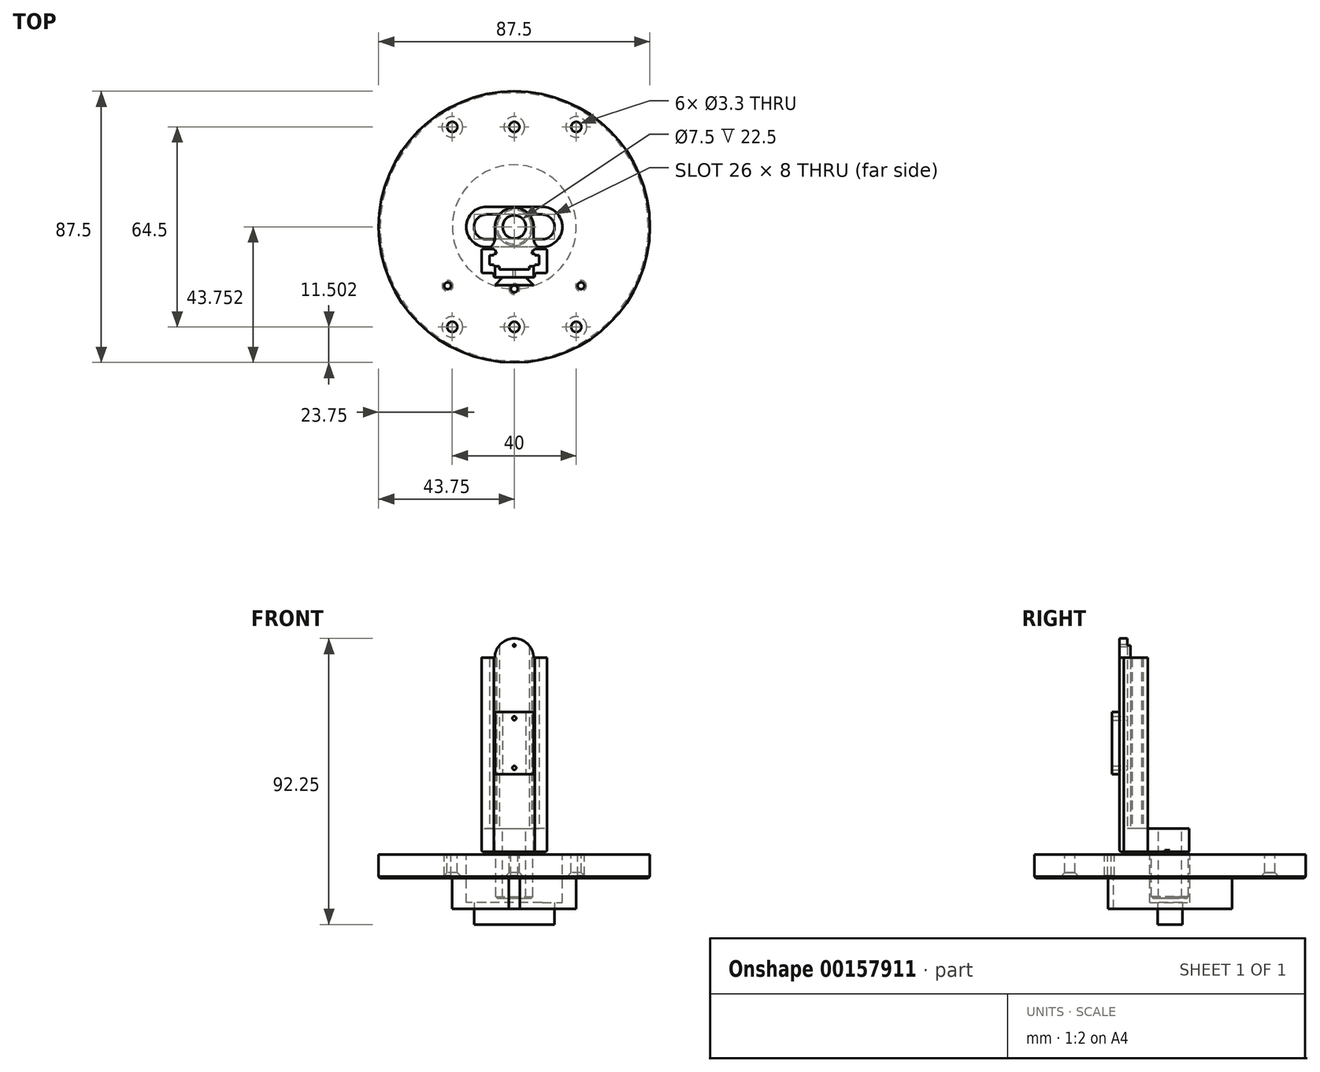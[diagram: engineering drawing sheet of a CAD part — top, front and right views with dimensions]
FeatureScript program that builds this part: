
annotation { "Feature Type Name" : "Feature", "Feature Type Description" : "" }
export const myFeature = defineFeature(function(context is Context, id is Id, definition is map)
    precondition{}
    {
        {
            var Q0;
            Q0=qCreatedBy(makeId("Top.planeOp"),FACE);
            var sketch = newSketch(context, id + "F0", { "sketchPlane" : qUnion([Q0])});
            skLineSegment(sketch, "E0.top", {"start": v(-6.65, -1.47) * mm, "end": v(-4.85, -1.47) * mm});
            skLineSegment(sketch, "E0.left", {"start": v(-8.05, 2.13) * mm, "end": v(-8.05, -0.97) * mm});
            skLineSegment(sketch, "E0.right", {"start": v(8.05, 2.13) * mm, "end": v(8.05, -0.97) * mm});
            skLineSegment(sketch, "E1", {"start": v(6.65, 2.63) * mm, "end": v(6.65, 2.13) * mm});
            skLineSegment(sketch, "E2", {"start": v(-6.65, 2.63) * mm, "end": v(-6.65, 2.13) * mm});
            skLineSegment(sketch, "E3", {"start": v(-4.85, -2.47) * mm, "end": v(4.85, -2.47) * mm});
            skLineSegment(sketch, "E4", {"start": v(6.65, 2.13) * mm, "end": v(8.05, 2.13) * mm});
            skLineSegment(sketch, "E5", {"start": v(-8.05, 2.13) * mm, "end": v(-6.65, 2.13) * mm});
            skLineSegment(sketch, "E6.MirrorCS", {"start": v(-8.05, -0.97) * mm, "end": v(-6.65, -0.97) * mm});
            skLineSegment(sketch, "E7.MirrorCS", {"start": v(6.65, -0.97) * mm, "end": v(8.05, -0.97) * mm});
            skLineSegment(sketch, "E8.trimOffspring", {"start": v(-6.65, -0.97) * mm, "end": v(-6.65, -1.47) * mm});
            skLineSegment(sketch, "E9.trimOffspring", {"start": v(6.65, -0.97) * mm, "end": v(6.65, -1.47) * mm});
            skLineSegment(sketch, "E10", {"start": v(-4.85, -1.47) * mm, "end": v(-4.85, -2.47) * mm});
            skLineSegment(sketch, "E11", {"start": v(4.85, -1.47) * mm, "end": v(4.85, -2.47) * mm});
            skLineSegment(sketch, "E12.trimOffspring", {"start": v(4.85, -1.47) * mm, "end": v(6.65, -1.47) * mm});
            skLineSegment(sketch, "E13", {"start": v(-10.55, 3.63) * mm, "end": v(-10.55, -3.14) * mm});
            skLineSegment(sketch, "E14", {"start": v(-10.05, 4.13) * mm, "end": v(-6.65, 4.13) * mm});
            skLineSegment(sketch, "E15", {"start": v(-6.15, -4.97) * mm, "end": v(6.15, -4.97) * mm});
            skLineSegment(sketch, "E16", {"start": v(10.55, -3.14) * mm, "end": v(10.55, 3.63) * mm});
            skLineSegment(sketch, "E17", {"start": v(10.05, 4.13) * mm, "end": v(6.65, 4.13) * mm});
            skPoint(sketch, "E18.visualSharp", {"position": v(10.55, 4.13) * mm});
            skArc(sketch, "E18.filletArc", {"start": v(10.55, 3.63) * mm, "mid": v(10.4, 3.99) * mm, "end": v(10.05, 4.13) * mm});
            skPoint(sketch, "E19.visualSharp", {"position": v(-10.55, 4.13) * mm});
            skArc(sketch, "E19.filletArc", {"start": v(-10.05, 4.13) * mm, "mid": v(-10.4, 3.99) * mm, "end": v(-10.55, 3.63) * mm});
            skLineSegment(sketch, "E20", {"start": v(-10.05, -3.64) * mm, "end": v(-7.15, -3.64) * mm});
            skLineSegment(sketch, "E21", {"start": v(6.65, -4.14) * mm, "end": v(6.65, -4.47) * mm});
            skLineSegment(sketch, "E22", {"start": v(-6.65, -4.14) * mm, "end": v(-6.65, -4.47) * mm});
            skLineSegment(sketch, "E23.trimOffspring", {"start": v(7.15, -3.64) * mm, "end": v(10.05, -3.64) * mm});
            skPoint(sketch, "E24.visualSharp", {"position": v(-10.55, -3.64) * mm});
            skArc(sketch, "E24.filletArc", {"start": v(-10.55, -3.14) * mm, "mid": v(-10.4, -3.49) * mm, "end": v(-10.05, -3.64) * mm});
            skPoint(sketch, "E25.visualSharp", {"position": v(-6.65, -3.64) * mm});
            skArc(sketch, "E25.filletArc", {"start": v(-6.65, -4.14) * mm, "mid": v(-6.8, -3.78) * mm, "end": v(-7.15, -3.64) * mm});
            skPoint(sketch, "E26.visualSharp", {"position": v(-6.65, -4.97) * mm});
            skArc(sketch, "E26.filletArc", {"start": v(-6.65, -4.47) * mm, "mid": v(-6.5, -4.82) * mm, "end": v(-6.15, -4.97) * mm});
            skPoint(sketch, "E27.visualSharp", {"position": v(6.65, -4.97) * mm});
            skArc(sketch, "E27.filletArc", {"start": v(6.15, -4.97) * mm, "mid": v(6.5, -4.82) * mm, "end": v(6.65, -4.47) * mm});
            skPoint(sketch, "E28.visualSharp", {"position": v(6.65, -3.64) * mm});
            skArc(sketch, "E28.filletArc", {"start": v(7.15, -3.64) * mm, "mid": v(6.8, -3.78) * mm, "end": v(6.65, -4.14) * mm});
            skPoint(sketch, "E29.visualSharp", {"position": v(10.55, -3.64) * mm});
            skArc(sketch, "E29.filletArc", {"start": v(10.05, -3.64) * mm, "mid": v(10.4, -3.49) * mm, "end": v(10.55, -3.14) * mm});
            skLineSegment(sketch, "E30", {"start": v(-6.65, 4.13) * mm, "end": v(-6.65, 3.88) * mm});
            skLineSegment(sketch, "E31", {"start": v(-6.65, 3.88) * mm, "end": v(-6.15, 3.88) * mm});
            skLineSegment(sketch, "E32", {"start": v(0, -2.47) * mm, "end": v(0, -1.47) * mm});
            skLineSegment(sketch, "E33.MirrorCS", {"start": v(6.65, 3.88) * mm, "end": v(6.15, 3.88) * mm});
            skLineSegment(sketch, "E34.MirrorCS", {"start": v(6.65, 4.13) * mm, "end": v(6.65, 3.88) * mm});
            skLineSegment(sketch, "E35", {"start": v(-6.65, 2.63) * mm, "end": v(-5.65, 2.63) * mm});
            skLineSegment(sketch, "E36", {"start": v(-6.15, 3.88) * mm, "end": v(-5.65, 2.63) * mm});
            skLineSegment(sketch, "E37.MirrorCS", {"start": v(6.65, 2.63) * mm, "end": v(5.65, 2.63) * mm});
            skLineSegment(sketch, "E38.MirrorCS", {"start": v(6.15, 3.88) * mm, "end": v(5.65, 2.63) * mm});
            skLineSegment(sketch, "E39", {"start": v(-8.05, 0.58) * mm, "end": v(-8.8, 0.58) * mm});
            skSolve(sketch);
        }
        {
            var Q0;
            Q0=makeQuery(id+"F0.imprint","IMPRINT",FACE,{"disambiguationData":[TD([[makeQuery(id+"F0.imprint","IMPRINT",EDGE,{"derivedFrom":sQuery(id+"F0.wireOp",EDGE,"E0.top")}),-1.0]])]});
            extrude(context, id + "F1", {"entities" : qUnion([Q0]), "depth" : 55 * mm, "symmetric" : true});
        }
        {
            var Q0;
            Q0=qCreatedBy(makeId("Top.planeOp"),FACE);
            var sketch = newSketch(context, id + "F2", { "sketchPlane" : qUnion([Q0])});
            skLineSegment(sketch, "E40.0", {"start": v(-3.75, -4.97) * mm, "end": v(3.75, -4.97) * mm});
            skLineSegment(sketch, "E41", {"start": v(-6.25, -7.47) * mm, "end": v(6.25, -7.47) * mm});
            skLineSegment(sketch, "E42", {"start": v(6.25, -7.47) * mm, "end": v(3.75, -4.97) * mm});
            skLineSegment(sketch, "E43.MirrorCS", {"start": v(-6.25, -7.47) * mm, "end": v(-3.75, -4.97) * mm});
            skPoint(sketch, "E44.orphan", {"position": v(6.15, -4.97) * mm});
            skPoint(sketch, "E45.orphan", {"position": v(-6.15, -4.97) * mm});
            skSolve(sketch);
        }
        {
            var Q0;
            Q0 = qSketchRegion(id + "F2", true);
            extrude(context, id + "F3", {"entities" : qUnion([Q0]), "operationType" : NewBodyOperationType.ADD, "depth" : 20 * mm, "symmetric" : true});
        }
        {
            var Q0;
            Q0=makeQuery(id+"F1.opExtrude","CAP_FACE",FACE,{"disambiguationData":[OSD([sQuery(id+"F0.wireOp",EDGE,"E0.top"),sQuery(id+"F0.wireOp",EDGE,"E0.left"),sQuery(id+"F0.wireOp",EDGE,"E0.right"),sQuery(id+"F0.wireOp",EDGE,"E1"),sQuery(id+"F0.wireOp",EDGE,"E2"),sQuery(id+"F0.wireOp",EDGE,"E3"),sQuery(id+"F0.wireOp",EDGE,"E4"),sQuery(id+"F0.wireOp",EDGE,"E5"),sQuery(id+"F0.wireOp",EDGE,"E6.MirrorCS"),sQuery(id+"F0.wireOp",EDGE,"E7.MirrorCS"),sQuery(id+"F0.wireOp",EDGE,"E8.trimOffspring"),sQuery(id+"F0.wireOp",EDGE,"E9.trimOffspring"),sQuery(id+"F0.wireOp",EDGE,"E10"),sQuery(id+"F0.wireOp",EDGE,"E11"),sQuery(id+"F0.wireOp",EDGE,"E12.trimOffspring"),sQuery(id+"F0.wireOp",EDGE,"E13"),sQuery(id+"F0.wireOp",EDGE,"E14"),sQuery(id+"F0.wireOp",EDGE,"E15"),sQuery(id+"F0.wireOp",EDGE,"E16"),sQuery(id+"F0.wireOp",EDGE,"E17"),sQuery(id+"F0.wireOp",EDGE,"E18.filletArc"),sQuery(id+"F0.wireOp",EDGE,"E19.filletArc"),sQuery(id+"F0.wireOp",EDGE,"E20"),sQuery(id+"F0.wireOp",EDGE,"E21"),sQuery(id+"F0.wireOp",EDGE,"E22"),sQuery(id+"F0.wireOp",EDGE,"E23.trimOffspring"),sQuery(id+"F0.wireOp",EDGE,"E24.filletArc"),sQuery(id+"F0.wireOp",EDGE,"E25.filletArc"),sQuery(id+"F0.wireOp",EDGE,"E26.filletArc"),sQuery(id+"F0.wireOp",EDGE,"E27.filletArc"),sQuery(id+"F0.wireOp",EDGE,"E28.filletArc"),sQuery(id+"F0.wireOp",EDGE,"E29.filletArc"),sQuery(id+"F0.wireOp",EDGE,"E30"),sQuery(id+"F0.wireOp",EDGE,"E31"),sQuery(id+"F0.wireOp",EDGE,"E33.MirrorCS"),sQuery(id+"F0.wireOp",EDGE,"E34.MirrorCS"),sQuery(id+"F0.wireOp",EDGE,"E35"),sQuery(id+"F0.wireOp",EDGE,"E36"),sQuery(id+"F0.wireOp",EDGE,"E37.MirrorCS"),sQuery(id+"F0.wireOp",EDGE,"E38.MirrorCS")])],"isStart":true});
            var sketch = newSketch(context, id + "F4", { "sketchPlane" : qUnion([Q0])});
            skLineSegment(sketch, "E46.0", {"start": v(-6.15, 4.97) * mm, "end": v(6.15, 4.97) * mm});
            skLineSegment(sketch, "E47.0", {"start": v(-10.05, 3.64) * mm, "end": v(-7.15, 3.64) * mm});
            skLineSegment(sketch, "E48.0", {"start": v(7.15, 3.64) * mm, "end": v(10.05, 3.64) * mm});
            skLineSegment(sketch, "E49.0", {"start": v(10.55, 3.14) * mm, "end": v(10.55, -3.63) * mm});
            skLineSegment(sketch, "E50.0", {"start": v(-10.55, -3.63) * mm, "end": v(-10.55, 3.14) * mm});
            skArc(sketch, "E51.0", {"start": v(6.15, 4.97) * mm, "mid": v(6.5, 4.82) * mm, "end": v(6.65, 4.47) * mm});
            skLineSegment(sketch, "E52.0", {"start": v(6.65, 4.14) * mm, "end": v(6.65, 4.47) * mm});
            skArc(sketch, "E53.0", {"start": v(7.15, 3.64) * mm, "mid": v(6.8, 3.78) * mm, "end": v(6.65, 4.14) * mm});
            skArc(sketch, "E54.0", {"start": v(-6.65, 4.47) * mm, "mid": v(-6.5, 4.82) * mm, "end": v(-6.15, 4.97) * mm});
            skLineSegment(sketch, "E55.0", {"start": v(-6.65, 4.14) * mm, "end": v(-6.65, 4.47) * mm});
            skArc(sketch, "E56.0", {"start": v(-6.65, 4.14) * mm, "mid": v(-6.8, 3.78) * mm, "end": v(-7.15, 3.64) * mm});
            skArc(sketch, "E57.0", {"start": v(-10.55, 3.14) * mm, "mid": v(-10.4, 3.49) * mm, "end": v(-10.05, 3.64) * mm});
            skArc(sketch, "E58.0", {"start": v(-10.05, -4.13) * mm, "mid": v(-10.4, -3.99) * mm, "end": v(-10.55, -3.63) * mm});
            skArc(sketch, "E59.0", {"start": v(10.05, 3.64) * mm, "mid": v(10.4, 3.49) * mm, "end": v(10.55, 3.14) * mm});
            skArc(sketch, "E60.0", {"start": v(10.55, -3.63) * mm, "mid": v(10.4, -3.99) * mm, "end": v(10.05, -4.13) * mm});
            skCircle(sketch, "E61", {"center": v(0, -11.28) * mm, "radius": 3.75 * mm});
            skCircle(sketch, "E62", {"center": v(0, -11.28) * mm, "radius": 6.25 * mm});
            skLineSegment(sketch, "E63", {"start": v(-6.25, -11.28) * mm, "end": v(-6.25, -7.63) * mm});
            skLineSegment(sketch, "E64", {"start": v(6.25, -11.28) * mm, "end": v(6.25, -7.63) * mm});
            skLineSegment(sketch, "E65", {"start": v(-10.05, -4.13) * mm, "end": v(-9.75, -4.13) * mm});
            skLineSegment(sketch, "E66.trimOffspring", {"start": v(9.75, -4.13) * mm, "end": v(10.05, -4.13) * mm});
            skPoint(sketch, "E67.visualSharp", {"position": v(-6.25, -4.13) * mm});
            skArc(sketch, "E67.filletArc", {"start": v(-6.25, -7.63) * mm, "mid": v(-7.28, -5.16) * mm, "end": v(-9.75, -4.13) * mm});
            skPoint(sketch, "E68.visualSharp", {"position": v(6.25, -4.13) * mm});
            skArc(sketch, "E68.filletArc", {"start": v(9.75, -4.13) * mm, "mid": v(7.28, -5.16) * mm, "end": v(6.25, -7.63) * mm});
            skSolve(sketch);
        }
        {
            var Q0;
            Q0 = qSketchRegion(id + "F4", true);
            extrude(context, id + "F5", {"entities" : qUnion([Q0]), "operationType" : NewBodyOperationType.ADD, "depth" : 7.5 * mm});
        }
        {
            var Q0;
            Q0=makeQuery(id+"F5.opExtrude","CAP_FACE",FACE,{"disambiguationData":[OSD([sQuery(id+"F4.wireOp",EDGE,"E46.0"),sQuery(id+"F4.wireOp",EDGE,"E47.0"),sQuery(id+"F4.wireOp",EDGE,"E48.0"),sQuery(id+"F4.wireOp",EDGE,"E49.0"),sQuery(id+"F4.wireOp",EDGE,"E50.0"),sQuery(id+"F4.wireOp",EDGE,"E51.0"),sQuery(id+"F4.wireOp",EDGE,"E52.0"),sQuery(id+"F4.wireOp",EDGE,"E53.0"),sQuery(id+"F4.wireOp",EDGE,"E54.0"),sQuery(id+"F4.wireOp",EDGE,"E55.0"),sQuery(id+"F4.wireOp",EDGE,"E56.0"),sQuery(id+"F4.wireOp",EDGE,"E57.0"),sQuery(id+"F4.wireOp",EDGE,"E58.0"),sQuery(id+"F4.wireOp",EDGE,"E59.0"),sQuery(id+"F4.wireOp",EDGE,"E60.0"),sQuery(id+"F4.wireOp",EDGE,"E61"),sQuery(id+"F4.wireOp",EDGE,"E62"),sQuery(id+"F4.wireOp",EDGE,"E63"),sQuery(id+"F4.wireOp",EDGE,"E64"),sQuery(id+"F4.wireOp",EDGE,"E65"),sQuery(id+"F4.wireOp",EDGE,"E66.trimOffspring"),sQuery(id+"F4.wireOp",EDGE,"E67.filletArc"),sQuery(id+"F4.wireOp",EDGE,"E68.filletArc")])],"isStart":false});
            var sketch = newSketch(context, id + "F6", { "sketchPlane" : qUnion([Q0])});
            skCircle(sketch, "E69.0", {"center": v(0, -11.28) * mm, "radius": 3.75 * mm});
            skCircle(sketch, "E70", {"center": v(0, -11.28) * mm, "radius": 6 * mm});
            skSolve(sketch);
        }
        {
            var Q0;
            Q0 = qSketchRegion(id + "F6", true);
            extrude(context, id + "F7", {"entities" : qUnion([Q0]), "operationType" : NewBodyOperationType.ADD, "depth" : 15 * mm});
        }
        {
            var Q0;
            Q0=makeQuery(id+"F5.opExtrude","CAP_EDGE",EDGE,{"disambiguationData":[OSD([sQuery(id+"F4.wireOp",EDGE,"E49.0")])],"isStart":false});
            fillet(context, id + "F8", {"entities" : qUnion([Q0]), "radius" : 0.5 * mm, "tangentPropagation" : true, "allowEdgeOverflow" : false});
        }
        {
            var Q0;
            Q0=makeQuery(id+"F7.opExtrude","CAP_EDGE",EDGE,{"disambiguationData":[OSD([sQuery(id+"F6.wireOp",EDGE,"E70")])],"isStart":false});
            chamfer(context, id + "F9", {"entities" : qUnion([Q0]), "width" : 0.5 * mm, "tangentPropagation" : true});
        }
        {
            var Q0;
            Q0=makeQuery(id+"F1.opExtrude","CAP_FACE",FACE,{"disambiguationData":[OSD([sQuery(id+"F0.wireOp",EDGE,"E0.top"),sQuery(id+"F0.wireOp",EDGE,"E0.left"),sQuery(id+"F0.wireOp",EDGE,"E0.right"),sQuery(id+"F0.wireOp",EDGE,"E1"),sQuery(id+"F0.wireOp",EDGE,"E2"),sQuery(id+"F0.wireOp",EDGE,"E3"),sQuery(id+"F0.wireOp",EDGE,"E4"),sQuery(id+"F0.wireOp",EDGE,"E5"),sQuery(id+"F0.wireOp",EDGE,"E6.MirrorCS"),sQuery(id+"F0.wireOp",EDGE,"E7.MirrorCS"),sQuery(id+"F0.wireOp",EDGE,"E8.trimOffspring"),sQuery(id+"F0.wireOp",EDGE,"E9.trimOffspring"),sQuery(id+"F0.wireOp",EDGE,"E10"),sQuery(id+"F0.wireOp",EDGE,"E11"),sQuery(id+"F0.wireOp",EDGE,"E12.trimOffspring"),sQuery(id+"F0.wireOp",EDGE,"E13"),sQuery(id+"F0.wireOp",EDGE,"E14"),sQuery(id+"F0.wireOp",EDGE,"E15"),sQuery(id+"F0.wireOp",EDGE,"E16"),sQuery(id+"F0.wireOp",EDGE,"E17"),sQuery(id+"F0.wireOp",EDGE,"E18.filletArc"),sQuery(id+"F0.wireOp",EDGE,"E19.filletArc"),sQuery(id+"F0.wireOp",EDGE,"E20"),sQuery(id+"F0.wireOp",EDGE,"E21"),sQuery(id+"F0.wireOp",EDGE,"E22"),sQuery(id+"F0.wireOp",EDGE,"E23.trimOffspring"),sQuery(id+"F0.wireOp",EDGE,"E24.filletArc"),sQuery(id+"F0.wireOp",EDGE,"E25.filletArc"),sQuery(id+"F0.wireOp",EDGE,"E26.filletArc"),sQuery(id+"F0.wireOp",EDGE,"E27.filletArc"),sQuery(id+"F0.wireOp",EDGE,"E28.filletArc"),sQuery(id+"F0.wireOp",EDGE,"E29.filletArc"),sQuery(id+"F0.wireOp",EDGE,"E30"),sQuery(id+"F0.wireOp",EDGE,"E31"),sQuery(id+"F0.wireOp",EDGE,"E33.MirrorCS"),sQuery(id+"F0.wireOp",EDGE,"E34.MirrorCS"),sQuery(id+"F0.wireOp",EDGE,"E35"),sQuery(id+"F0.wireOp",EDGE,"E36"),sQuery(id+"F0.wireOp",EDGE,"E37.MirrorCS"),sQuery(id+"F0.wireOp",EDGE,"E38.MirrorCS")])],"isStart":false});
            var sketch = newSketch(context, id + "F10", { "sketchPlane" : qUnion([Q0])});
            skLineSegment(sketch, "E71", {"start": v(6.25, -4.96) * mm, "end": v(6.25, -1.47) * mm});
            skLineSegment(sketch, "E72.0", {"start": v(-6.15, -4.97) * mm, "end": v(6.15, -4.97) * mm});
            skLineSegment(sketch, "E73.0", {"start": v(-4.85, -2.47) * mm, "end": v(4.85, -2.47) * mm});
            skLineSegment(sketch, "E74.0", {"start": v(4.85, -1.47) * mm, "end": v(6.65, -1.47) * mm});
            skLineSegment(sketch, "E75", {"start": v(4.85, -1.47) * mm, "end": v(4.85, -2.47) * mm});
            skLineSegment(sketch, "E76.MirrorCS", {"start": v(-4.85, -1.47) * mm, "end": v(-6.65, -1.47) * mm});
            skLineSegment(sketch, "E77.MirrorCS", {"start": v(-4.85, -1.47) * mm, "end": v(-4.85, -2.47) * mm});
            skLineSegment(sketch, "E78.MirrorCS", {"start": v(-6.25, -4.96) * mm, "end": v(-6.25, -1.47) * mm});
            skArc(sketch, "E79.0", {"start": v(6.15, -4.97) * mm, "mid": v(6.2, -4.97) * mm, "end": v(6.25, -4.96) * mm});
            skArc(sketch, "E80.0", {"start": v(-6.25, -4.96) * mm, "mid": v(-6.2, -4.97) * mm, "end": v(-6.15, -4.97) * mm});
            skPoint(sketch, "E81.orphan", {"position": v(-6.25, 0.76) * mm});
            skPoint(sketch, "E82.orphan", {"position": v(6.25, 0.76) * mm});
            skPoint(sketch, "E83.orphan", {"position": v(6.25, -5.79) * mm});
            skPoint(sketch, "E84.orphan", {"position": v(-6.25, -5.79) * mm});
            skPoint(sketch, "E85.orphan", {"position": v(-6.65, -4.47) * mm});
            skPoint(sketch, "E86.orphan", {"position": v(6.65, -4.47) * mm});
            skSolve(sketch);
        }
        {
            var Q0;
            Q0 = qSketchRegion(id + "F10", true);
            extrude(context, id + "F11", {"entities" : qUnion([Q0]), "operationType" : NewBodyOperationType.ADD, "depth" : 6.25 * mm});
        }
        {
            var Q0;
            Q0=makeQuery(id+"F11.boolean.opBoolean","MERGE",FACE,{"derivedFrom":[makeQuery(id+"F5.boolean.opBoolean","MERGE",FACE,{"derivedFrom":[makeQuery(id+"F1.opExtrude","SWEPT_FACE",FACE,{"disambiguationData":[OSD([sQuery(id+"F0.wireOp",EDGE,"E15")])]}),makeQuery(id+"F5.opExtrude","SWEPT_FACE",FACE,{"disambiguationData":[OSD([sQuery(id+"F4.wireOp",EDGE,"E46.0")])]})]}),makeQuery(id+"F11.opExtrude","SWEPT_FACE",FACE,{"disambiguationData":[OSD([sQuery(id+"F10.wireOp",EDGE,"E72.0")])]})]});
            var sketch = newSketch(context, id + "F12", { "sketchPlane" : qUnion([Q0])});
            skArc(sketch, "E87", {"start": v(6.25, 27.5) * mm, "mid": v(0, 33.75) * mm, "end": v(-6.25, 27.5) * mm});
            skPoint(sketch, "E87.centerSnap0", {"position": v(0, 33.75) * mm});
            skLineSegment(sketch, "E88", {"start": v(7.15, 27.5) * mm, "end": v(6.25, 27.5) * mm});
            skLineSegment(sketch, "E89", {"start": v(-7.18, 27.5) * mm, "end": v(-7.18, 34.65) * mm});
            skLineSegment(sketch, "E90", {"start": v(-7.18, 34.65) * mm, "end": v(7.15, 34.65) * mm});
            skLineSegment(sketch, "E91", {"start": v(7.15, 34.65) * mm, "end": v(7.15, 27.5) * mm});
            skPoint(sketch, "E92.orphan", {"position": v(6.15, 33.75) * mm});
            skPoint(sketch, "E93.0.start.orphan", {"position": v(-6.15, 33.75) * mm});
            skLineSegment(sketch, "E94.trimOffspring", {"start": v(-6.25, 27.5) * mm, "end": v(-7.18, 27.5) * mm});
            skPoint(sketch, "E95.0.end.orphan", {"position": v(10.05, 27.5) * mm});
            skSolve(sketch);
        }
        {
            var Q0;
            Q0 = qSketchRegion(id + "F12", true);
            extrude(context, id + "F13", {"entities" : qUnion([Q0]), "operationType" : NewBodyOperationType.REMOVE, "endBound" : BoundingType.THROUGH_ALL, "oppositeDirection" : true, "depth" : 25 * mm});
        }
        {
            var Q0;
            Q0=makeQuery(id+"F11.boolean.opBoolean","MERGE",FACE,{"derivedFrom":[makeQuery(id+"F5.boolean.opBoolean","MERGE",FACE,{"derivedFrom":[makeQuery(id+"F1.opExtrude","SWEPT_FACE",FACE,{"disambiguationData":[OSD([sQuery(id+"F0.wireOp",EDGE,"E15")])]}),makeQuery(id+"F5.opExtrude","SWEPT_FACE",FACE,{"disambiguationData":[OSD([sQuery(id+"F4.wireOp",EDGE,"E46.0")])]})]}),makeQuery(id+"F11.opExtrude","SWEPT_FACE",FACE,{"disambiguationData":[OSD([sQuery(id+"F10.wireOp",EDGE,"E72.0")])]})]});
            var sketch = newSketch(context, id + "F14", { "sketchPlane" : qUnion([Q0])});
            skLineSegment(sketch, "E96.0", {"start": v(7.15, 27.5) * mm, "end": v(10.05, 27.5) * mm});
            skPoint(sketch, "E97", {"position": v(0, 31.5) * mm});
            skSolve(sketch);
        }
        {
            var Q0;
            Q0=sQuery(id+"F14.wireOp",VERTEX,"E97");
            var Q1;
            Q1=makeQuery(id+"F1.opExtrude","SWEPT_BODY",BODY,{"disambiguationData":[OSD([sQuery(id+"F0.wireOp",EDGE,"E0.top"),sQuery(id+"F0.wireOp",EDGE,"E0.left"),sQuery(id+"F0.wireOp",EDGE,"E0.right"),sQuery(id+"F0.wireOp",EDGE,"E1"),sQuery(id+"F0.wireOp",EDGE,"E2"),sQuery(id+"F0.wireOp",EDGE,"E3"),sQuery(id+"F0.wireOp",EDGE,"E4"),sQuery(id+"F0.wireOp",EDGE,"E5"),sQuery(id+"F0.wireOp",EDGE,"E6.MirrorCS"),sQuery(id+"F0.wireOp",EDGE,"E7.MirrorCS"),sQuery(id+"F0.wireOp",EDGE,"E8.trimOffspring"),sQuery(id+"F0.wireOp",EDGE,"E9.trimOffspring"),sQuery(id+"F0.wireOp",EDGE,"E10"),sQuery(id+"F0.wireOp",EDGE,"E11"),sQuery(id+"F0.wireOp",EDGE,"E12.trimOffspring"),sQuery(id+"F0.wireOp",EDGE,"E13"),sQuery(id+"F0.wireOp",EDGE,"E14"),sQuery(id+"F0.wireOp",EDGE,"E15"),sQuery(id+"F0.wireOp",EDGE,"E16"),sQuery(id+"F0.wireOp",EDGE,"E17"),sQuery(id+"F0.wireOp",EDGE,"E18.filletArc"),sQuery(id+"F0.wireOp",EDGE,"E19.filletArc"),sQuery(id+"F0.wireOp",EDGE,"E20"),sQuery(id+"F0.wireOp",EDGE,"E21"),sQuery(id+"F0.wireOp",EDGE,"E22"),sQuery(id+"F0.wireOp",EDGE,"E23.trimOffspring"),sQuery(id+"F0.wireOp",EDGE,"E24.filletArc"),sQuery(id+"F0.wireOp",EDGE,"E25.filletArc"),sQuery(id+"F0.wireOp",EDGE,"E26.filletArc"),sQuery(id+"F0.wireOp",EDGE,"E27.filletArc"),sQuery(id+"F0.wireOp",EDGE,"E28.filletArc"),sQuery(id+"F0.wireOp",EDGE,"E29.filletArc"),sQuery(id+"F0.wireOp",EDGE,"E30"),sQuery(id+"F0.wireOp",EDGE,"E31"),sQuery(id+"F0.wireOp",EDGE,"E33.MirrorCS"),sQuery(id+"F0.wireOp",EDGE,"E34.MirrorCS"),sQuery(id+"F0.wireOp",EDGE,"E35"),sQuery(id+"F0.wireOp",EDGE,"E36"),sQuery(id+"F0.wireOp",EDGE,"E37.MirrorCS"),sQuery(id+"F0.wireOp",EDGE,"E38.MirrorCS")])]});
            hole(context, id + "F15", {"style" : HoleStyle.SIMPLE, "endStyle" : HoleEndStyle.THROUGH, "holeDiameter" : 0.75 * mm, "locations" : qUnion([Q0]), "scope" : qUnion([Q1]), "isTappedThrough" : true, "startStyle" : HoleStartStyle.SKETCH});
        }
        {
            var Q0;
            Q0=makeQuery(id+"F3.opExtrude","SWEPT_FACE",FACE,{"disambiguationData":[OSD([sQuery(id+"F2.wireOp",EDGE,"E41")])]});
            var sketch = newSketch(context, id + "F16", { "sketchPlane" : qUnion([Q0])});
            skPoint(sketch, "E98", {"position": v(0, 8) * mm});
            skPoint(sketch, "E99.MirrorP", {"position": v(0, -8) * mm});
            skSolve(sketch);
        }
        {
            var Q0;
            Q0=sQuery(id+"F16.wireOp",VERTEX,"E98");
            var Q1;
            Q1=sQuery(id+"F16.wireOp",VERTEX,"E99.MirrorP");
            var Q2;
            Q2=makeQuery(id+"F1.opExtrude","SWEPT_BODY",BODY,{"disambiguationData":[OSD([sQuery(id+"F0.wireOp",EDGE,"E0.top"),sQuery(id+"F0.wireOp",EDGE,"E0.left"),sQuery(id+"F0.wireOp",EDGE,"E0.right"),sQuery(id+"F0.wireOp",EDGE,"E1"),sQuery(id+"F0.wireOp",EDGE,"E2"),sQuery(id+"F0.wireOp",EDGE,"E3"),sQuery(id+"F0.wireOp",EDGE,"E4"),sQuery(id+"F0.wireOp",EDGE,"E5"),sQuery(id+"F0.wireOp",EDGE,"E6.MirrorCS"),sQuery(id+"F0.wireOp",EDGE,"E7.MirrorCS"),sQuery(id+"F0.wireOp",EDGE,"E8.trimOffspring"),sQuery(id+"F0.wireOp",EDGE,"E9.trimOffspring"),sQuery(id+"F0.wireOp",EDGE,"E10"),sQuery(id+"F0.wireOp",EDGE,"E11"),sQuery(id+"F0.wireOp",EDGE,"E12.trimOffspring"),sQuery(id+"F0.wireOp",EDGE,"E13"),sQuery(id+"F0.wireOp",EDGE,"E14"),sQuery(id+"F0.wireOp",EDGE,"E15"),sQuery(id+"F0.wireOp",EDGE,"E16"),sQuery(id+"F0.wireOp",EDGE,"E17"),sQuery(id+"F0.wireOp",EDGE,"E18.filletArc"),sQuery(id+"F0.wireOp",EDGE,"E19.filletArc"),sQuery(id+"F0.wireOp",EDGE,"E20"),sQuery(id+"F0.wireOp",EDGE,"E21"),sQuery(id+"F0.wireOp",EDGE,"E22"),sQuery(id+"F0.wireOp",EDGE,"E23.trimOffspring"),sQuery(id+"F0.wireOp",EDGE,"E24.filletArc"),sQuery(id+"F0.wireOp",EDGE,"E25.filletArc"),sQuery(id+"F0.wireOp",EDGE,"E26.filletArc"),sQuery(id+"F0.wireOp",EDGE,"E27.filletArc"),sQuery(id+"F0.wireOp",EDGE,"E28.filletArc"),sQuery(id+"F0.wireOp",EDGE,"E29.filletArc"),sQuery(id+"F0.wireOp",EDGE,"E30"),sQuery(id+"F0.wireOp",EDGE,"E31"),sQuery(id+"F0.wireOp",EDGE,"E33.MirrorCS"),sQuery(id+"F0.wireOp",EDGE,"E34.MirrorCS"),sQuery(id+"F0.wireOp",EDGE,"E35"),sQuery(id+"F0.wireOp",EDGE,"E36"),sQuery(id+"F0.wireOp",EDGE,"E37.MirrorCS"),sQuery(id+"F0.wireOp",EDGE,"E38.MirrorCS")])]});
            hole(context, id + "F17", {"style" : HoleStyle.SIMPLE, "endStyle" : HoleEndStyle.THROUGH, "holeDiameter" : 1.25 * mm, "locations" : qUnion([Q0, Q1]), "scope" : qUnion([Q2]), "isTappedThrough" : true, "startStyle" : HoleStartStyle.SKETCH});
        }
        {
            var Q0;
            Q0=qCreatedBy(makeId("Top.planeOp"),FACE);
            cPlane(context, id + "F18", {"entities" : qUnion([Q0]), "cplaneType" : CPlaneType.OFFSET, "offset" : 36 * mm, "oppositeDirection" : true, "width" : 150 * mm, "height" : 150 * mm});
        }
        {
            var Q0;
            Q0=qCreatedBy(id+"F18.planeOp",FACE);
            var sketch = newSketch(context, id + "F19", { "sketchPlane" : qUnion([Q0])});
            skCircle(sketch, "E100.0", {"center": v(0, 11.28) * mm, "radius": 3.75 * mm});
            skCircle(sketch, "E101", {"center": v(0, 11.28) * mm, "radius": 43.75 * mm});
            skCircle(sketch, "E102", {"center": v(0, 11.28) * mm, "radius": 6.5 * mm});
            skLineSegment(sketch, "E103.bottom", {"start": v(9, 17.78) * mm, "end": v(-9, 17.78) * mm});
            skLineSegment(sketch, "E103.top", {"start": v(9, 4.78) * mm, "end": v(-9, 4.78) * mm});
            skArc(sketch, "E104", {"start": v(9, 4.78) * mm, "mid": v(15.5, 11.28) * mm, "end": v(9, 17.78) * mm});
            skArc(sketch, "E105.MirrorCS", {"start": v(-9, 4.78) * mm, "mid": v(-15.5, 11.28) * mm, "end": v(-9, 17.78) * mm});
            skSolve(sketch);
        }
        {
            var Q0;
            Q0 = qSketchRegion(id + "F19", true);
            extrude(context, id + "F20", {"entities" : qUnion([Q0]), "oppositeDirection" : true, "depth" : 7.5 * mm});
        }
        {
            var Q0;
            Q0=makeQuery(id+"F20.opExtrude","CAP_FACE",FACE,{"disambiguationData":[OSD([sQuery(id+"F19.wireOp",EDGE,"E101"),sQuery(id+"F19.wireOp",EDGE,"E103.bottom"),sQuery(id+"F19.wireOp",EDGE,"E103.top"),sQuery(id+"F19.wireOp",EDGE,"E104"),sQuery(id+"F19.wireOp",EDGE,"E105.MirrorCS")])],"isStart":false});
            var sketch = newSketch(context, id + "F21", { "sketchPlane" : qUnion([Q0])});
            skCircle(sketch, "E106", {"center": v(0, -11.28) * mm, "radius": 20 * mm});
            skLineSegment(sketch, "E107.0", {"start": v(9, -4.78) * mm, "end": v(-9, -4.78) * mm});
            skArc(sketch, "E108.0", {"start": v(9, -4.78) * mm, "mid": v(15.5, -11.28) * mm, "end": v(9, -17.78) * mm});
            skLineSegment(sketch, "E109.0", {"start": v(9, -17.78) * mm, "end": v(-9, -17.78) * mm});
            skArc(sketch, "E110.0", {"start": v(-9, -4.78) * mm, "mid": v(-15.5, -11.28) * mm, "end": v(-9, -17.78) * mm});
            skSolve(sketch);
        }
        {
            var Q0;
            Q0 = qSketchRegion(id + "F21", true);
            extrude(context, id + "F22", {"entities" : qUnion([Q0]), "operationType" : NewBodyOperationType.ADD, "depth" : 10 * mm});
        }
        {
            var Q0;
            Q0=makeQuery(id+"F22.opExtrude","CAP_FACE",FACE,{"disambiguationData":[OSD([sQuery(id+"F21.wireOp",EDGE,"E106"),sQuery(id+"F21.wireOp",EDGE,"E107.0"),sQuery(id+"F21.wireOp",EDGE,"E108.0"),sQuery(id+"F21.wireOp",EDGE,"E109.0"),sQuery(id+"F21.wireOp",EDGE,"E110.0")])],"isStart":false});
            var sketch = newSketch(context, id + "F23", { "sketchPlane" : qUnion([Q0])});
            skArc(sketch, "E111.0", {"start": v(9, -4.78) * mm, "mid": v(15.5, -11.28) * mm, "end": v(9, -17.78) * mm});
            skLineSegment(sketch, "E112.0", {"start": v(9, -4.78) * mm, "end": v(-9, -4.78) * mm});
            skLineSegment(sketch, "E113.0", {"start": v(9, -17.78) * mm, "end": v(-9, -17.78) * mm});
            skArc(sketch, "E114.0", {"start": v(-9, -4.78) * mm, "mid": v(-15.5, -11.28) * mm, "end": v(-9, -17.78) * mm});
            skArc(sketch, "E115.0", {"start": v(9, -7.28) * mm, "mid": v(13, -11.28) * mm, "end": v(9, -15.28) * mm});
            skLineSegment(sketch, "E116.0", {"start": v(9, -7.28) * mm, "end": v(-9, -7.28) * mm});
            skArc(sketch, "E117.0", {"start": v(-9, -7.28) * mm, "mid": v(-13, -11.28) * mm, "end": v(-9, -15.28) * mm});
            skLineSegment(sketch, "E118", {"start": v(9, -15.28) * mm, "end": v(-9, -15.28) * mm});
            skSolve(sketch);
        }
        {
            var Q0;
            Q0 = qSketchRegion(id + "F23", true);
            extrude(context, id + "F24", {"entities" : qUnion([Q0]), "operationType" : NewBodyOperationType.ADD, "oppositeDirection" : true, "depth" : 2 * mm});
        }
        {
            var Q0;
            Q0=makeQuery(id+"F24.boolean.opBoolean","MERGE",FACE,{"derivedFrom":[makeQuery(id+"F22.opExtrude","CAP_FACE",FACE,{"disambiguationData":[OSD([sQuery(id+"F21.wireOp",EDGE,"E106"),sQuery(id+"F21.wireOp",EDGE,"E107.0"),sQuery(id+"F21.wireOp",EDGE,"E108.0"),sQuery(id+"F21.wireOp",EDGE,"E109.0"),sQuery(id+"F21.wireOp",EDGE,"E110.0")])],"isStart":false}),makeQuery(id+"F24.opExtrude","CAP_FACE",FACE,{"disambiguationData":[OSD([sQuery(id+"F23.wireOp",EDGE,"E111.0"),sQuery(id+"F23.wireOp",EDGE,"E112.0"),sQuery(id+"F23.wireOp",EDGE,"E113.0"),sQuery(id+"F23.wireOp",EDGE,"E114.0"),sQuery(id+"F23.wireOp",EDGE,"E115.0"),sQuery(id+"F23.wireOp",EDGE,"E116.0"),sQuery(id+"F23.wireOp",EDGE,"E117.0"),sQuery(id+"F23.wireOp",EDGE,"E118")])],"isStart":true})]});
            var sketch = newSketch(context, id + "F25", { "sketchPlane" : qUnion([Q0])});
            skArc(sketch, "E119.0", {"start": v(9, -7.28) * mm, "mid": v(13, -11.28) * mm, "end": v(9, -15.28) * mm});
            skLineSegment(sketch, "E120.0", {"start": v(9, -15.28) * mm, "end": v(-9, -15.28) * mm});
            skArc(sketch, "E121.0", {"start": v(-9, -7.28) * mm, "mid": v(-13, -11.28) * mm, "end": v(-9, -15.28) * mm});
            skLineSegment(sketch, "E122.0", {"start": v(9, -7.28) * mm, "end": v(-9, -7.28) * mm});
            skArc(sketch, "E123.0", {"start": v(9, -2.28) * mm, "mid": v(18, -11.28) * mm, "end": v(9, -20.28) * mm});
            skLineSegment(sketch, "E123.1", {"start": v(9, -2.28) * mm, "end": v(-9, -2.28) * mm});
            skArc(sketch, "E123.2", {"start": v(-9, -2.28) * mm, "mid": v(-18, -11.28) * mm, "end": v(-9, -20.28) * mm});
            skLineSegment(sketch, "E123.3", {"start": v(9, -20.28) * mm, "end": v(-9, -20.28) * mm});
            skSolve(sketch);
        }
        {
            var Q0;
            Q0=makeQuery(id+"F25.imprint","IMPRINT",FACE,{"disambiguationData":[TD([[makeQuery(id+"F25.imprint","IMPRINT",EDGE,{"derivedFrom":sQuery(id+"F25.wireOp",EDGE,"E119.0")}),1.0]])]});
            extrude(context, id + "F26", {"entities" : qUnion([Q0]), "operationType" : NewBodyOperationType.ADD, "depth" : 5 * mm});
        }
        {
            var Q0;
            Q0=makeQuery(id+"F20.opExtrude","CAP_FACE",FACE,{"disambiguationData":[OSD([sQuery(id+"F19.wireOp",EDGE,"E101"),sQuery(id+"F19.wireOp",EDGE,"E103.bottom"),sQuery(id+"F19.wireOp",EDGE,"E103.top"),sQuery(id+"F19.wireOp",EDGE,"E104"),sQuery(id+"F19.wireOp",EDGE,"E105.MirrorCS")])],"isStart":false});
            var sketch = newSketch(context, id + "F27", { "sketchPlane" : qUnion([Q0])});
            skPoint(sketch, "E124", {"position": v(0, -43.53) * mm});
            skPoint(sketch, "E125", {"position": v(20, -43.53) * mm});
            skPoint(sketch, "E126.MirrorP", {"position": v(-20, -43.53) * mm});
            skPoint(sketch, "E127", {"position": v(0, -11.28) * mm});
            skLineSegment(sketch, "E128", {"start": v(0, -11.28) * mm, "end": v(17.92, -11.28) * mm});
            skPoint(sketch, "E129.MirrorP", {"position": v(20, 20.97) * mm});
            skPoint(sketch, "E130.MirrorP", {"position": v(0, 20.97) * mm});
            skPoint(sketch, "E131.MirrorP", {"position": v(-20, 20.97) * mm});
            skSolve(sketch);
        }
        {
            var Q0;
            Q0=sQuery(id+"F27.wireOp",VERTEX,"E125");
            var Q1;
            Q1=sQuery(id+"F27.wireOp",VERTEX,"E124");
            var Q2;
            Q2=sQuery(id+"F27.wireOp",VERTEX,"E126.MirrorP");
            var Q3;
            Q3=sQuery(id+"F27.wireOp",VERTEX,"E129.MirrorP");
            var Q4;
            Q4=sQuery(id+"F27.wireOp",VERTEX,"E130.MirrorP");
            var Q5;
            Q5=sQuery(id+"F27.wireOp",VERTEX,"E131.MirrorP");
            var Q6;
            Q6=makeQuery(id+"F20.opExtrude","SWEPT_BODY",BODY,{"disambiguationData":[OSD([sQuery(id+"F19.wireOp",EDGE,"E101"),sQuery(id+"F19.wireOp",EDGE,"E103.bottom"),sQuery(id+"F19.wireOp",EDGE,"E103.top"),sQuery(id+"F19.wireOp",EDGE,"E104"),sQuery(id+"F19.wireOp",EDGE,"E105.MirrorCS")])]});
            hole(context, id + "F28", {"style" : HoleStyle.C_SINK, "endStyle" : HoleEndStyle.THROUGH, "standardTappedOrClearance" : lookupTablePath({ "standard" : "ISO", "fit" : "Normal", "size" : "M3", "type" : "Clearance" }), "standardBlindInLast" : lookupTablePath({ "fit" : "Standard", "standard" : "ISO", "size" : "M3", "type" : "Clearance" }), "holeDiameter" : 3.3 * mm, "cSinkDiameter" : 6.72 * mm, "cSinkAngle" : 90 * degree, "locations" : qUnion([Q0, Q1, Q2, Q3, Q4, Q5]), "scope" : qUnion([Q6]), "isTappedThrough" : true, "startStyle" : HoleStartStyle.SKETCH});
        }
        {
            var Q0;
            Q0=makeQuery(id+"F20.opExtrude","CAP_FACE",FACE,{"disambiguationData":[OSD([sQuery(id+"F19.wireOp",EDGE,"E101"),sQuery(id+"F19.wireOp",EDGE,"E103.bottom"),sQuery(id+"F19.wireOp",EDGE,"E103.top"),sQuery(id+"F19.wireOp",EDGE,"E104"),sQuery(id+"F19.wireOp",EDGE,"E105.MirrorCS")])],"isStart":false});
            var sketch = newSketch(context, id + "F29", { "sketchPlane" : qUnion([Q0])});
            skPoint(sketch, "E132", {"position": v(21.5, 7.72) * mm});
            skPoint(sketch, "E133.MirrorP", {"position": v(-21.5, 7.72) * mm});
            skCircle(sketch, "E134.0", {"center": v(0, -11.28) * mm, "radius": 3.75 * mm});
            skLineSegment(sketch, "E135", {"start": v(-21.5, 7.72) * mm, "end": v(21.5, 7.72) * mm});
            skPoint(sketch, "E136", {"position": v(0, 8.72) * mm});
            skSolve(sketch);
        }
        {
            var Q0;
            Q0=sQuery(id+"F29.wireOp",VERTEX,"E133.MirrorP");
            var Q1;
            Q1=sQuery(id+"F29.wireOp",VERTEX,"E136");
            var Q2;
            Q2=sQuery(id+"F29.wireOp",VERTEX,"E132");
            var Q3;
            Q3=makeQuery(id+"F20.opExtrude","SWEPT_BODY",BODY,{"disambiguationData":[OSD([sQuery(id+"F19.wireOp",EDGE,"E101"),sQuery(id+"F19.wireOp",EDGE,"E103.bottom"),sQuery(id+"F19.wireOp",EDGE,"E103.top"),sQuery(id+"F19.wireOp",EDGE,"E104"),sQuery(id+"F19.wireOp",EDGE,"E105.MirrorCS")])]});
            hole(context, id + "F30", {"style" : HoleStyle.C_SINK, "endStyle" : HoleEndStyle.THROUGH, "holeDiameter" : 2.2 * mm, "cSinkDiameter" : 3.5 * mm, "cSinkAngle" : 90 * degree, "locations" : qUnion([Q0, Q1, Q2]), "scope" : qUnion([Q3]), "isTappedThrough" : true, "startStyle" : HoleStartStyle.SKETCH});
        }
        {
            var Q0;
            Q0=makeQuery(id+"F20.opExtrude","CAP_FACE",FACE,{"disambiguationData":[OSD([sQuery(id+"F19.wireOp",EDGE,"E101"),sQuery(id+"F19.wireOp",EDGE,"E103.bottom"),sQuery(id+"F19.wireOp",EDGE,"E103.top"),sQuery(id+"F19.wireOp",EDGE,"E104"),sQuery(id+"F19.wireOp",EDGE,"E105.MirrorCS")])],"isStart":false});
            var sketch = newSketch(context, id + "F31", { "sketchPlane" : qUnion([Q0])});
            skArc(sketch, "E137.0", {"start": v(1.75, 8.64) * mm, "mid": v(0, 10.47) * mm, "end": v(-1.75, 8.64) * mm});
            skCircle(sketch, "E138", {"center": v(0, 8.72) * mm, "radius": 1.75 * mm});
            skSolve(sketch);
        }
        {
            var Q0;
            Q0 = qSketchRegion(id + "F31", true);
            extrude(context, id + "F32", {"entities" : qUnion([Q0]), "operationType" : NewBodyOperationType.REMOVE, "endBound" : BoundingType.THROUGH_ALL, "depth" : 25 * mm});
        }
        {
            var Q0;
            Q0=makeQuery(id+"F20.opExtrude","CAP_EDGE",EDGE,{"disambiguationData":[OSD([sQuery(id+"F19.wireOp",EDGE,"E101")])],"isStart":false});
            chamfer(context, id + "F33", {"entities" : qUnion([Q0]), "width" : 0.5 * mm, "tangentPropagation" : true});
        }
    });
